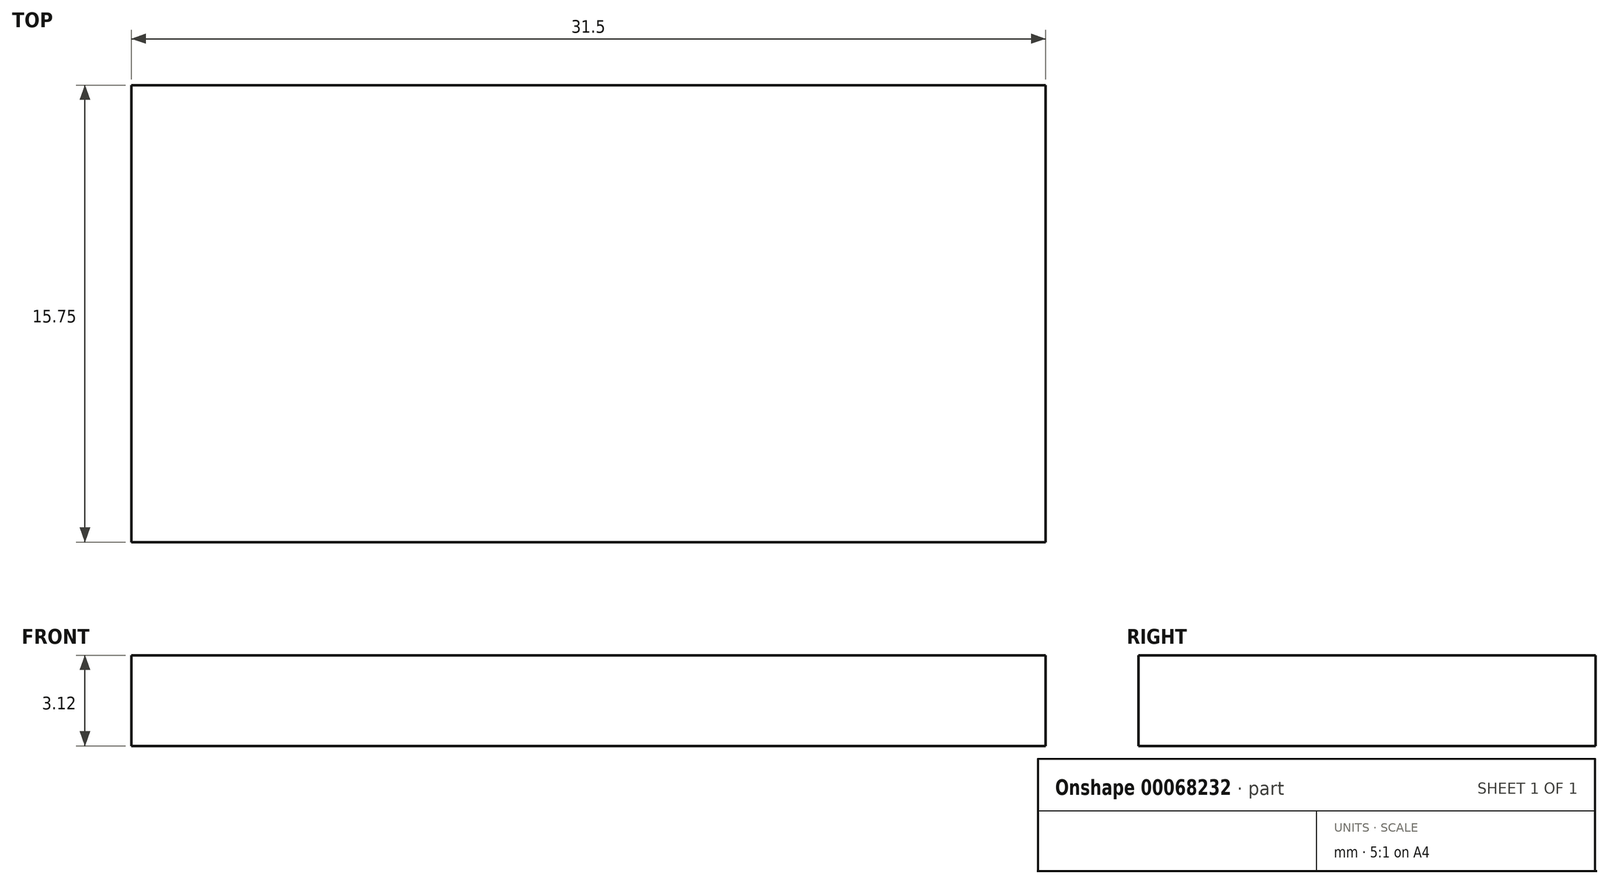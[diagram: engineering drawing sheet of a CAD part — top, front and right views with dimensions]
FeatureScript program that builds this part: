
annotation { "Feature Type Name" : "Feature", "Feature Type Description" : "" }
export const myFeature = defineFeature(function(context is Context, id is Id, definition is map)
    precondition{}
    {
        {
            var Q0;
            Q0=qCreatedBy(makeId("Top.planeOp"),FACE);
            var sketch = newSketch(context, id + "F0", { "sketchPlane" : qUnion([Q0])});
            skLineSegment(sketch, "E0.bottom", {"start": v(0, 0) * mm, "end": v(31.5, 0) * mm});
            skLineSegment(sketch, "E0.top", {"start": v(0, 15.75) * mm, "end": v(31.5, 15.75) * mm});
            skLineSegment(sketch, "E0.left", {"start": v(0, 0) * mm, "end": v(0, 15.75) * mm});
            skLineSegment(sketch, "E0.right", {"start": v(31.5, 0) * mm, "end": v(31.5, 15.75) * mm});
            skSolve(sketch);
        }
        {
            var Q0;
            Q0=makeQuery(id+"F0.imprint","IMPRINT",FACE,{"disambiguationData":[TD([[makeQuery(id+"F0.imprint","IMPRINT",EDGE,{"derivedFrom":sQuery(id+"F0.wireOp",EDGE,"E0.bottom")}),1.0]])]});
            extrude(context, id + "F1", {"entities" : qUnion([Q0]), "depth" : 3.12 * mm});
        }
    });
